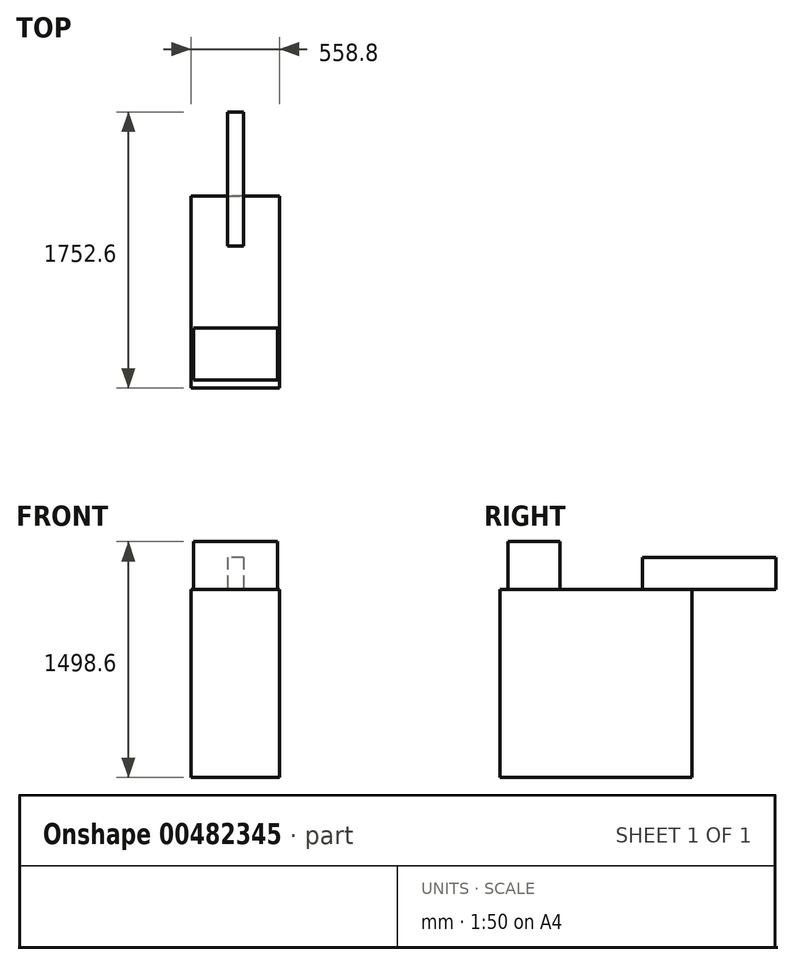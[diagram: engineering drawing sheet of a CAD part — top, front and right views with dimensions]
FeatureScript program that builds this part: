
annotation { "Feature Type Name" : "Feature", "Feature Type Description" : "" }
export const myFeature = defineFeature(function(context is Context, id is Id, definition is map)
    precondition{}
    {
        {
            var Q0;
            Q0=qCreatedBy(makeId("Top.planeOp"),FACE);
            var sketch = newSketch(context, id + "F0", { "sketchPlane" : qUnion([Q0])});
            skLineSegment(sketch, "E0.bottom", {"start": v(0, 0) * mm, "end": v(558.8, 0) * mm});
            skLineSegment(sketch, "E0.top", {"start": v(0, 1219.2) * mm, "end": v(558.8, 1219.2) * mm});
            skLineSegment(sketch, "E0.left", {"start": v(0, 0) * mm, "end": v(0, 1219.2) * mm});
            skLineSegment(sketch, "E0.right", {"start": v(558.8, 0) * mm, "end": v(558.8, 1219.2) * mm});
            skLineSegment(sketch, "E1.bottom", {"start": v(12.7, 381) * mm, "end": v(546.1, 381) * mm});
            skLineSegment(sketch, "E1.top", {"start": v(12.7, 50.8) * mm, "end": v(546.1, 50.8) * mm});
            skLineSegment(sketch, "E1.left", {"start": v(12.7, 381) * mm, "end": v(12.7, 50.8) * mm});
            skLineSegment(sketch, "E1.right", {"start": v(546.1, 381) * mm, "end": v(546.1, 50.8) * mm});
            skLineSegment(sketch, "E2.bottom", {"start": v(330.2, 902.37) * mm, "end": v(228.6, 902.37) * mm});
            skLineSegment(sketch, "E2.top", {"start": v(330.2, 1752.6) * mm, "end": v(228.6, 1752.6) * mm});
            skLineSegment(sketch, "E2.left", {"start": v(330.2, 902.37) * mm, "end": v(330.2, 1752.6) * mm});
            skLineSegment(sketch, "E2.right", {"start": v(228.6, 902.37) * mm, "end": v(228.6, 1752.6) * mm});
            skLineSegment(sketch, "E3", {"start": v(279.4, 1219.2) * mm, "end": v(279.4, 902.37) * mm, "construction": true});
            skSolve(sketch);
        }
        {
            var Q0;
            Q0=makeQuery(id+"F0.imprint","IMPRINT",FACE,{"disambiguationData":[TD([[makeQuery(id+"F0.imprint","IMPRINT",EDGE,{"derivedFrom":sQuery(id+"F0.wireOp",EDGE,"E0.bottom")}),1.0]])]});
            extrude(context, id + "F1", {"entities" : qUnion([Q0]), "depth" : 1193.8 * mm, "offsetDistance" : 25.4 * mm});
        }
        {
            var Q0;
            {var subQ5=sQuery(id+"F0.wireOp",EDGE,"E2.top");Q0=makeQuery(id+"F0.imprint","IMPRINT",FACE,{"disambiguationData":[TD([[makeQuery(id+"F0.imprint","IMPRINT",EDGE,{"derivedFrom":subQ5}),1.0]])]});}
            var Q1;
            {var subQ5=sQuery(id+"F0.wireOp",EDGE,"E2.bottom");Q1=makeQuery(id+"F0.imprint","IMPRINT",FACE,{"disambiguationData":[TD([[makeQuery(id+"F0.imprint","IMPRINT",EDGE,{"derivedFrom":subQ5}),-1.0]])]});}
            extrude(context, id + "F2", {"entities" : qUnion([Q0, Q1]), "operationType" : NewBodyOperationType.ADD, "depth" : 1397 * mm, "offsetDistance" : 25.4 * mm});
        }
        {
            var Q0;
            Q0=makeQuery(id+"F0.imprint","IMPRINT",FACE,{"disambiguationData":[TD([[makeQuery(id+"F0.imprint","IMPRINT",EDGE,{"derivedFrom":sQuery(id+"F0.wireOp",EDGE,"E1.bottom")}),-1.0]])]});
            extrude(context, id + "F3", {"entities" : qUnion([Q0]), "operationType" : NewBodyOperationType.ADD, "depth" : 1498.6 * mm, "offsetDistance" : 25.4 * mm});
        }
        {
            var Q0;
            Q0=makeQuery(id+"F2.opExtrude","SWEPT_FACE",FACE,{"disambiguationData":[OSD([sQuery(id+"F0.wireOp",EDGE,"E2.right")])]});
            var sketch = newSketch(context, id + "F4", { "sketchPlane" : qUnion([Q0])});
            skLineSegment(sketch, "E4.bottom", {"start": v(-1219.2, 1193.8) * mm, "end": v(-1752.6, 1193.8) * mm});
            skLineSegment(sketch, "E4.top", {"start": v(-1219.2, 0) * mm, "end": v(-1752.6, 0) * mm});
            skLineSegment(sketch, "E4.left", {"start": v(-1219.2, 1193.8) * mm, "end": v(-1219.2, 0) * mm});
            skLineSegment(sketch, "E4.right", {"start": v(-1752.6, 1193.8) * mm, "end": v(-1752.6, 0) * mm});
            skSolve(sketch);
        }
        {
            var Q0;
            Q0 = qSketchRegion(id + "F4", true);
            extrude(context, id + "F5", {"entities" : qUnion([Q0]), "operationType" : NewBodyOperationType.REMOVE, "endBound" : BoundingType.THROUGH_ALL, "oppositeDirection" : true, "depth" : 25.4 * mm, "offsetDistance" : 25.4 * mm});
        }
    });
